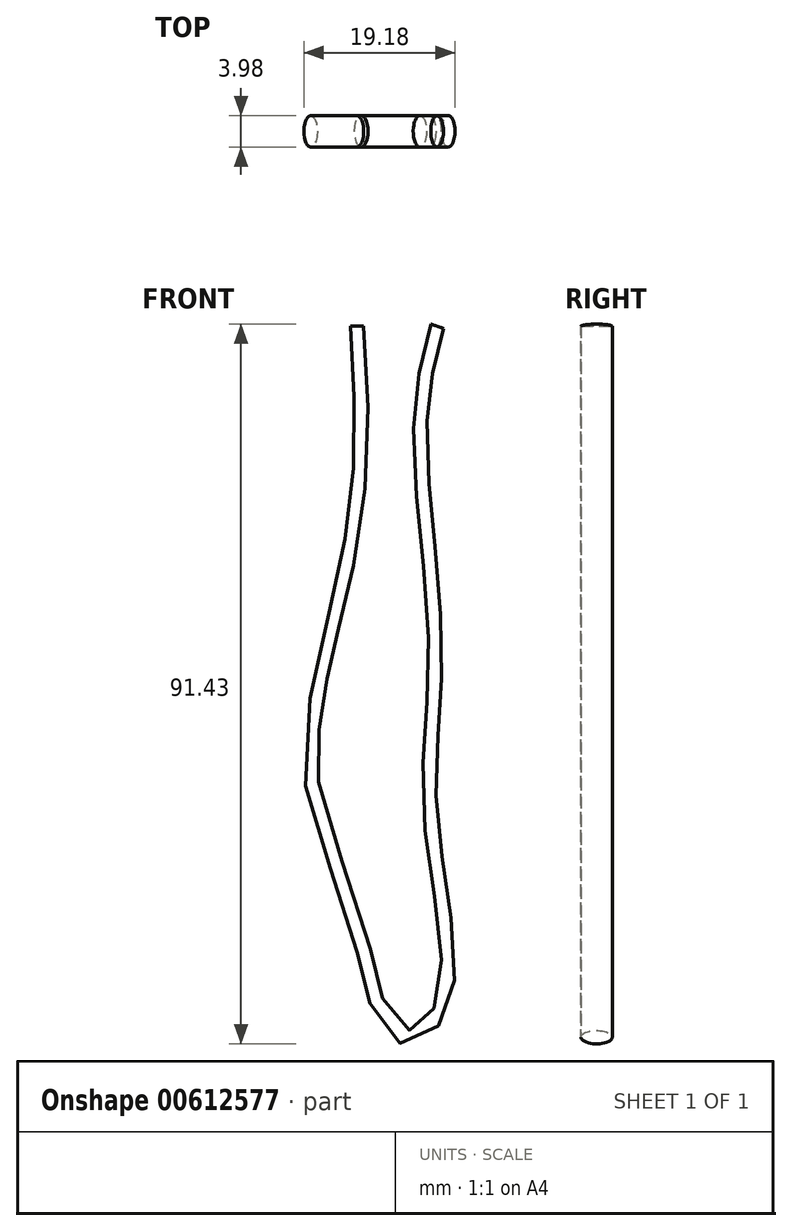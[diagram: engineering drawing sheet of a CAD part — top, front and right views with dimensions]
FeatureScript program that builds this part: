
annotation { "Feature Type Name" : "Feature", "Feature Type Description" : "" }
export const myFeature = defineFeature(function(context is Context, id is Id, definition is map)
    precondition{}
    {
        {
            var Q0;
            Q0=qCreatedBy(makeId("Front.planeOp"),FACE);
            var sketch = newSketch(context, id + "F0", { "sketchPlane" : qUnion([Q0])});
            skLineSegment(sketch, "E0", {"start": v(0, 0) * mm, "end": v(0, -90) * mm, "construction": true});
            skLineSegment(sketch, "E1", {"start": v(0, 0) * mm, "end": v(-5, 0) * mm, "construction": true});
            skLineSegment(sketch, "E2.MirrorCS", {"start": v(0, 0) * mm, "end": v(5, 0) * mm, "construction": true});
            skFitSpline(sketch, "E3", {"points": [v(-5, 0) * mm, v(-5, -22.49) * mm, v(-9.38, -43.54) * mm, v(-10.49, -59.61) * mm, v(-5, -75.96) * mm, v(0, -90) * mm, v(5.58, -86.48) * mm, v(4.2, -62.94) * mm, v(4.75, -41.33) * mm, v(2.8, -14.18) * mm, v(5, 0) * mm], "startDerivative": vector(14.12, -189.19) * mm, "endDerivative": vector(47.7, 184.7) * mm});
            skSolve(sketch);
        }
        {
            var Q0;
            Q0=qCreatedBy(makeId("Top.planeOp"),FACE);
            var sketch = newSketch(context, id + "F1", { "sketchPlane" : qUnion([Q0])});
            skEllipse(sketch, "E4", {"center": v(-5.09, 0) * mm, "majorRadius": 2 * mm, "minorRadius": 0.85 * mm, "majorAxis": v(0, -1)});
            skSolve(sketch);
        }
        {
            var Q0;
            Q0=makeQuery(id+"F1.imprint","IMPRINT",FACE,{"disambiguationData":[TD([[makeQuery(id+"F1.imprint","IMPRINT",EDGE,{"derivedFrom":sQuery(id+"F1.wireOp",EDGE,"E4")}),1.0]])]});
            var Q1;
            Q1=sQuery(id+"F0.wireOp",EDGE,"E3");
            sweep(context, id + "F2", {"profiles" : qUnion([Q0]), "path" : qUnion([Q1])});
        }
    });
